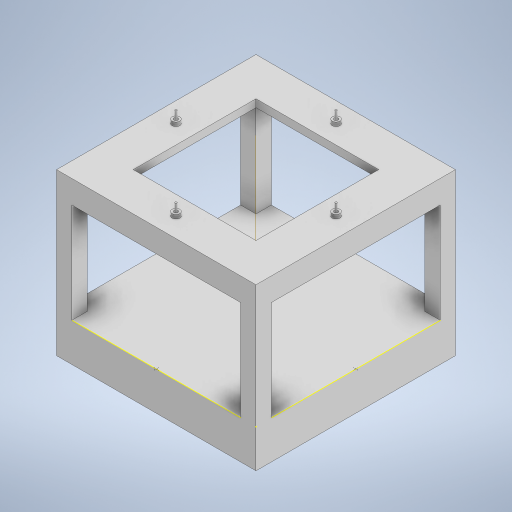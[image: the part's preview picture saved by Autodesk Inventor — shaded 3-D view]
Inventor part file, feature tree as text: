
AUTODESK INVENTOR PART (.ipt)
format: ipt  version: 2023 (Build 270158000, 158)  size: 309,760 bytes
history: native  units: in
note: dims shown in document units (in); Inventor stores cm internally (conversion verified against a paired STEP export)
features: sketch x8, extrude x7, plane x1, other x1, pattern_circular x1
ambient origin geometry x8: Origin, YZ Plane, XZ Plane, XY Plane, X Axis, Y Axis, Z Axis, Center Point
bodies: Solid1 (feature_tree)
feature tree (18):
  extrude  "Extrusion1"  Depth=10.2362in
  sketch  "Sketch2"  dims[d2=7.874in d3=0.0in d4=0.7874in]
  sketch  "Sketch3"  dims[d5=0.7874in d6=0.7874in]
  extrude  "Extrusion2"  Depth=0.7874in
  extrude  "Extrusion3"  Depth=0.7874in
  plane  "Work Plane1"
  extrude  "Extrusion4"  Depth=0.7874in
  extrude  "Extrusion5"  Depth=0.7874in
  sketch  "Sketch6"  dims[d11=1.9685in d12=5.9055in d13=0.0in]
  extrude  "Extrusion7"  Depth=5.9055in TaperAngle=0.0deg
  sketch  "Sketch8"  dims[d21=10.2362in d22=0.0in d23=1.9685in d24=1.9685in d25=1.9685in d26=1.9685in d27=0.3937in d28=0.0in d29=5.1181in d30=5.1181in d31=7.6772in d32=8.7598in d33=8.2185in d37=0.3937in d38=0.1969in d39=0.0in d43=0.0984in d44=0.5906in d45=0.0in d46=1.5748in d47=360.0deg]
  other  "Work Axis2"
  extrude  "Extrusion8"  [1 undecoded]
  pattern_circular  "Circular Pattern2"  Count=2  [1 undecoded]
  sketch  "Sketch1"  dims[d0=10.2362in d1=10.2362in]
  sketch  "Sketch4"  dims[d7=0.7874in d8=0.7874in]
  sketch  "Sketch5"  dims[d9=0.7874in d10=0.7874in]
  sketch  "Sketch7"  dims[d14=10.2362in d15=0.0in d16=-5.1181in d17=0.7874in d18=0.7874in d19=0.7874in d20=1.9685in]
note: 2 required parameter values undecoded (feature->parameter linkage not recoverable at this tier; creation-order binding heuristic only, values carry confidence <= 0.55)
